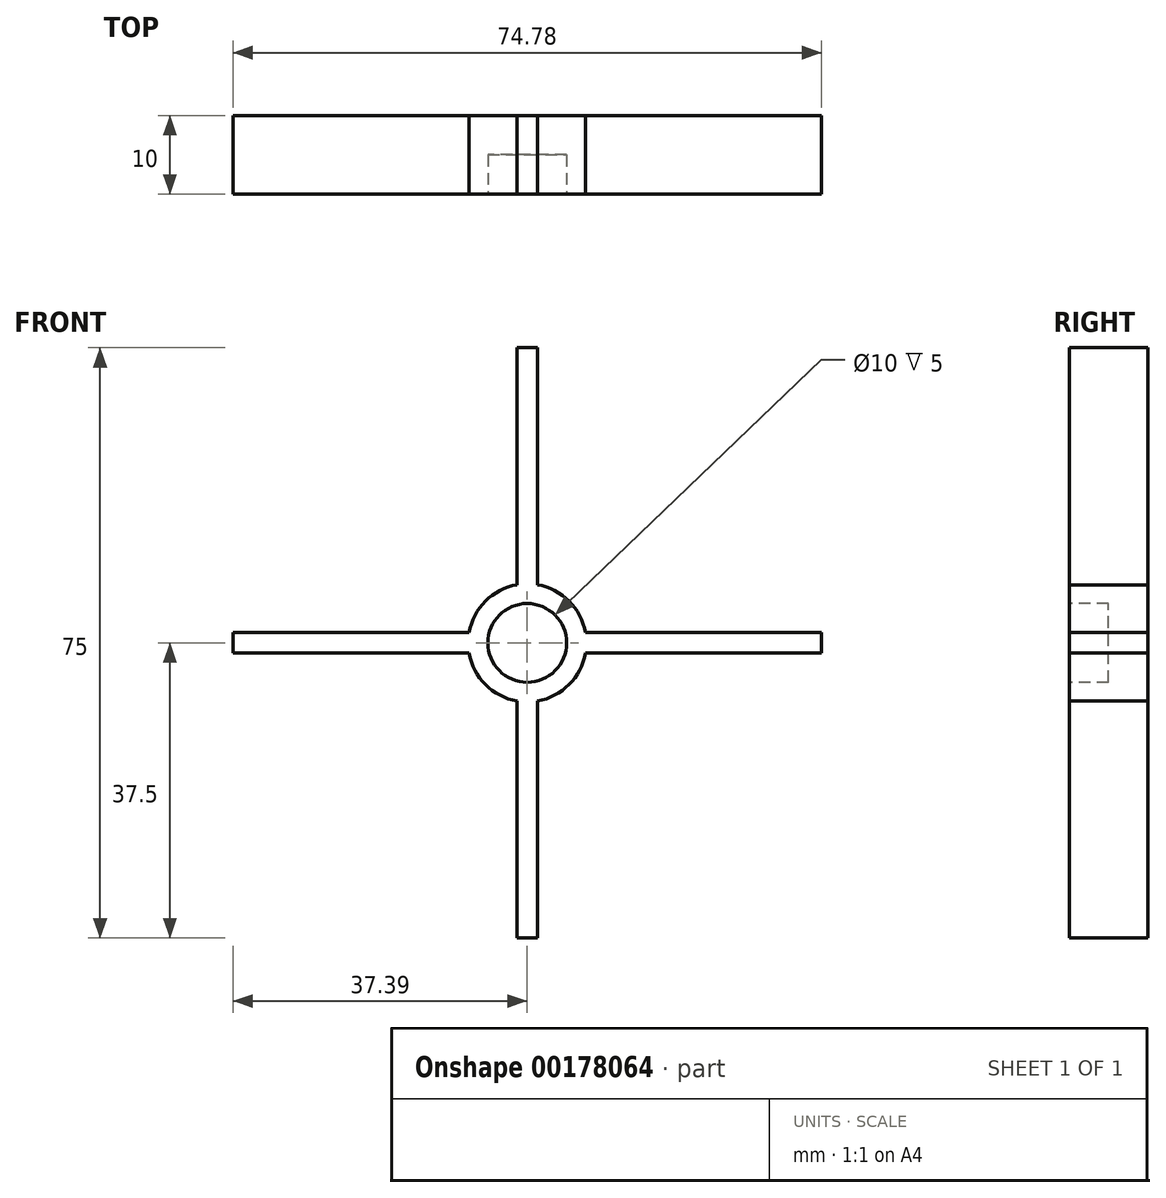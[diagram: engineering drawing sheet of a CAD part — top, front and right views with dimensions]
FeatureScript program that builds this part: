
annotation { "Feature Type Name" : "Feature", "Feature Type Description" : "" }
export const myFeature = defineFeature(function(context is Context, id is Id, definition is map)
    precondition{}
    {
        {
            var Q0;
            Q0=qCreatedBy(makeId("Front.planeOp"),FACE);
            var sketch = newSketch(context, id + "F0", { "sketchPlane" : qUnion([Q0])});
            skCircle(sketch, "E0", {"center": v(0, 0) * mm, "radius": 7.5 * mm});
            skLineSegment(sketch, "E1", {"start": v(-1.3, 7.39) * mm, "end": v(-1.3, 37.5) * mm});
            skLineSegment(sketch, "E2", {"start": v(-1.3, 37.5) * mm, "end": v(0, 37.5) * mm});
            skLineSegment(sketch, "E3", {"start": v(0, 0) * mm, "end": v(0, 7.5) * mm, "construction": true});
            skLineSegment(sketch, "E4.MirrorCS", {"start": v(1.3, 7.39) * mm, "end": v(1.3, 37.5) * mm});
            skLineSegment(sketch, "E5.MirrorCS", {"start": v(1.3, 37.5) * mm, "end": v(0, 37.5) * mm});
            skLineSegment(sketch, "E6", {"start": v(-7.5, 0) * mm, "end": v(7.5, 0) * mm, "construction": true});
            skLineSegment(sketch, "E7.MirrorCS", {"start": v(1.3, -7.39) * mm, "end": v(1.3, -37.5) * mm});
            skLineSegment(sketch, "E8.MirrorCS", {"start": v(-1.3, -7.39) * mm, "end": v(-1.3, -37.5) * mm});
            skLineSegment(sketch, "E9.MirrorCS", {"start": v(-1.3, -37.5) * mm, "end": v(0, -37.5) * mm});
            skLineSegment(sketch, "E10.MirrorCS", {"start": v(1.3, -37.5) * mm, "end": v(0, -37.5) * mm});
            skLineSegment(sketch, "E11", {"start": v(0, 0) * mm, "end": v(0, -7.5) * mm, "construction": true});
            skLineSegment(sketch, "E12", {"start": v(-7.39, 1.3) * mm, "end": v(-37.39, 1.3) * mm});
            skLineSegment(sketch, "E13", {"start": v(-37.39, 1.3) * mm, "end": v(-37.39, 0) * mm});
            skLineSegment(sketch, "E14.MirrorCS", {"start": v(-7.39, -1.3) * mm, "end": v(-37.39, -1.3) * mm});
            skLineSegment(sketch, "E15.MirrorCS", {"start": v(-37.39, -1.3) * mm, "end": v(-37.39, 0) * mm});
            skLineSegment(sketch, "E16.MirrorCS", {"start": v(7.39, 1.3) * mm, "end": v(37.39, 1.3) * mm});
            skLineSegment(sketch, "E17.MirrorCS", {"start": v(7.39, -1.3) * mm, "end": v(37.39, -1.3) * mm});
            skLineSegment(sketch, "E18.MirrorCS", {"start": v(37.39, 1.3) * mm, "end": v(37.39, 0) * mm});
            skLineSegment(sketch, "E19.MirrorCS", {"start": v(37.39, -1.3) * mm, "end": v(37.39, 0) * mm});
            skSolve(sketch);
        }
        {
            var Q0;
            Q0 = qSketchRegion(id + "F0", true);
            extrude(context, id + "F1", {"entities" : qUnion([Q0]), "depth" : 10 * mm});
        }
        {
            var Q0;
            Q0=makeQuery(id+"F1.opExtrude","CAP_FACE",FACE,{"disambiguationData":[OSD([sQuery(id+"F0.wireOp",EDGE,"E0"),sQuery(id+"F0.wireOp",EDGE,"E1"),sQuery(id+"F0.wireOp",EDGE,"E2"),sQuery(id+"F0.wireOp",EDGE,"E4.MirrorCS"),sQuery(id+"F0.wireOp",EDGE,"E5.MirrorCS"),sQuery(id+"F0.wireOp",EDGE,"E7.MirrorCS"),sQuery(id+"F0.wireOp",EDGE,"E8.MirrorCS"),sQuery(id+"F0.wireOp",EDGE,"E9.MirrorCS"),sQuery(id+"F0.wireOp",EDGE,"E10.MirrorCS"),sQuery(id+"F0.wireOp",EDGE,"E12"),sQuery(id+"F0.wireOp",EDGE,"E13"),sQuery(id+"F0.wireOp",EDGE,"E14.MirrorCS"),sQuery(id+"F0.wireOp",EDGE,"E15.MirrorCS"),sQuery(id+"F0.wireOp",EDGE,"E16.MirrorCS"),sQuery(id+"F0.wireOp",EDGE,"E17.MirrorCS"),sQuery(id+"F0.wireOp",EDGE,"E18.MirrorCS"),sQuery(id+"F0.wireOp",EDGE,"E19.MirrorCS")])],"isStart":false});
            var sketch = newSketch(context, id + "F2", { "sketchPlane" : qUnion([Q0])});
            skCircle(sketch, "E20", {"center": v(0, 0) * mm, "radius": 5 * mm});
            skSolve(sketch);
        }
        {
            var Q0;
            Q0 = qSketchRegion(id + "F2", true);
            extrude(context, id + "F3", {"entities" : qUnion([Q0]), "operationType" : NewBodyOperationType.REMOVE, "oppositeDirection" : true, "depth" : 5 * mm});
        }
    });
